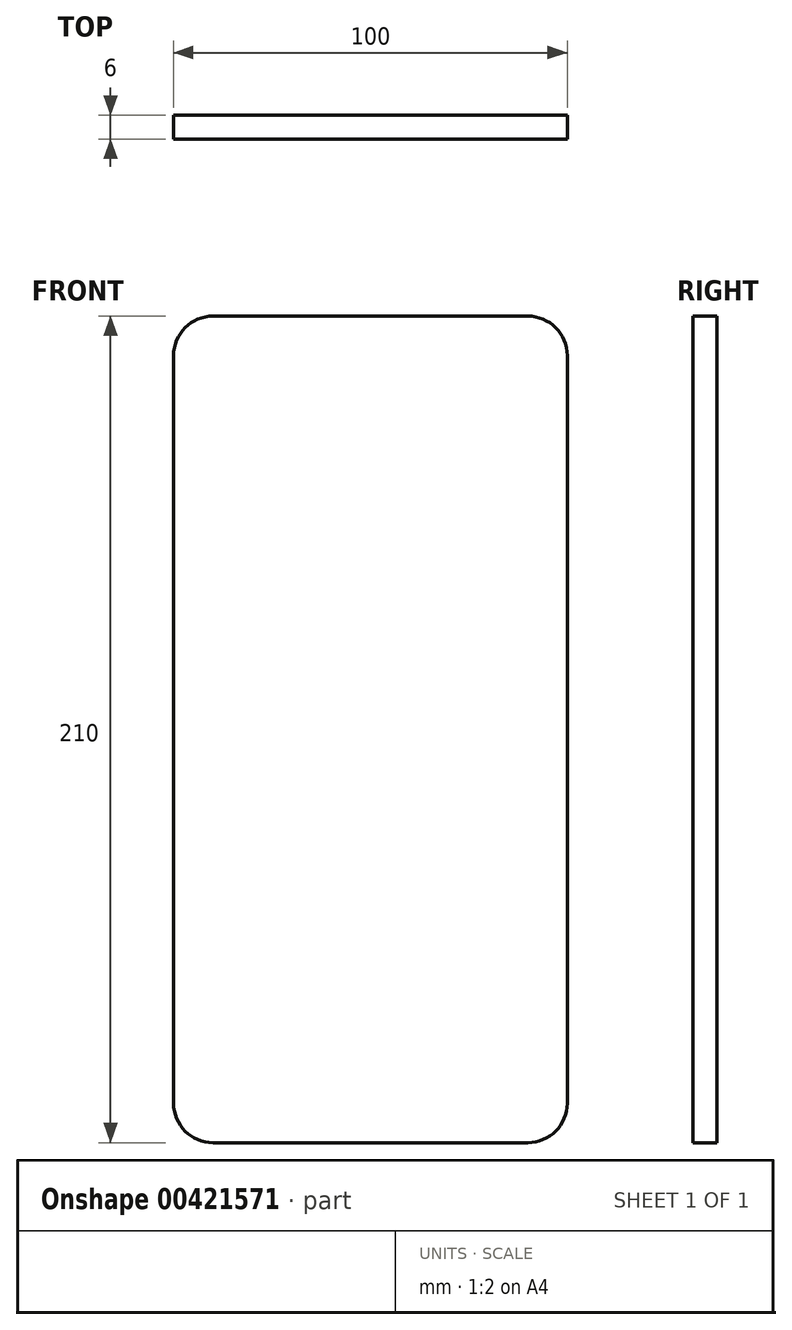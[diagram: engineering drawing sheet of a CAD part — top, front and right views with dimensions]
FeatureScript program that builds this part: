
annotation { "Feature Type Name" : "Feature", "Feature Type Description" : "" }
export const myFeature = defineFeature(function(context is Context, id is Id, definition is map)
    precondition{}
    {
        {
            var Q0;
            Q0=qCreatedBy(makeId("Front.planeOp"),FACE);
            var sketch = newSketch(context, id + "F0", { "sketchPlane" : qUnion([Q0])});
            skLineSegment(sketch, "E0.bottom", {"start": v(-50, 105) * mm, "end": v(50, 105) * mm});
            skLineSegment(sketch, "E0.top", {"start": v(-50, -105) * mm, "end": v(50, -105) * mm});
            skLineSegment(sketch, "E0.left", {"start": v(-50, 105) * mm, "end": v(-50, -105) * mm});
            skLineSegment(sketch, "E0.right", {"start": v(50, 105) * mm, "end": v(50, -105) * mm});
            skSolve(sketch);
        }
        {
            var Q0;
            Q0=qSketchRegion(id+"F0",true);
            extrude(context, id + "F1", {"entities" : qUnion([Q0]), "depth" : 6 * mm, "offsetDistance" : 25 * mm});
        }
        {
            var Q0;
            Q0=makeQuery(id+"F1.opExtrude","SWEPT_EDGE",EDGE,{"disambiguationData":[OSD([sQuery(id+"F0.wireOp",EDGE,"E0.top"),sQuery(id+"F0.wireOp",EDGE,"E0.left")])]});
            var Q1;
            Q1=makeQuery(id+"F1.opExtrude","SWEPT_EDGE",EDGE,{"disambiguationData":[OSD([sQuery(id+"F0.wireOp",EDGE,"E0.top"),sQuery(id+"F0.wireOp",EDGE,"E0.right")])]});
            fillet(context, id + "F2", {"entities" : qUnion([Q0, Q1]), "radius" : 10 * mm, "tangentPropagation" : true, "allowEdgeOverflow" : false});
        }
        {
            var Q0;
            Q0=makeQuery(id+"F1.opExtrude","SWEPT_EDGE",EDGE,{"disambiguationData":[OSD([sQuery(id+"F0.wireOp",EDGE,"E0.bottom"),sQuery(id+"F0.wireOp",EDGE,"E0.left")])]});
            var Q1;
            Q1=makeQuery(id+"F1.opExtrude","SWEPT_EDGE",EDGE,{"disambiguationData":[OSD([sQuery(id+"F0.wireOp",EDGE,"E0.bottom"),sQuery(id+"F0.wireOp",EDGE,"E0.right")])]});
            fillet(context, id + "F3", {"entities" : qUnion([Q0, Q1]), "radius" : 10 * mm, "tangentPropagation" : true, "allowEdgeOverflow" : false});
        }
    });
